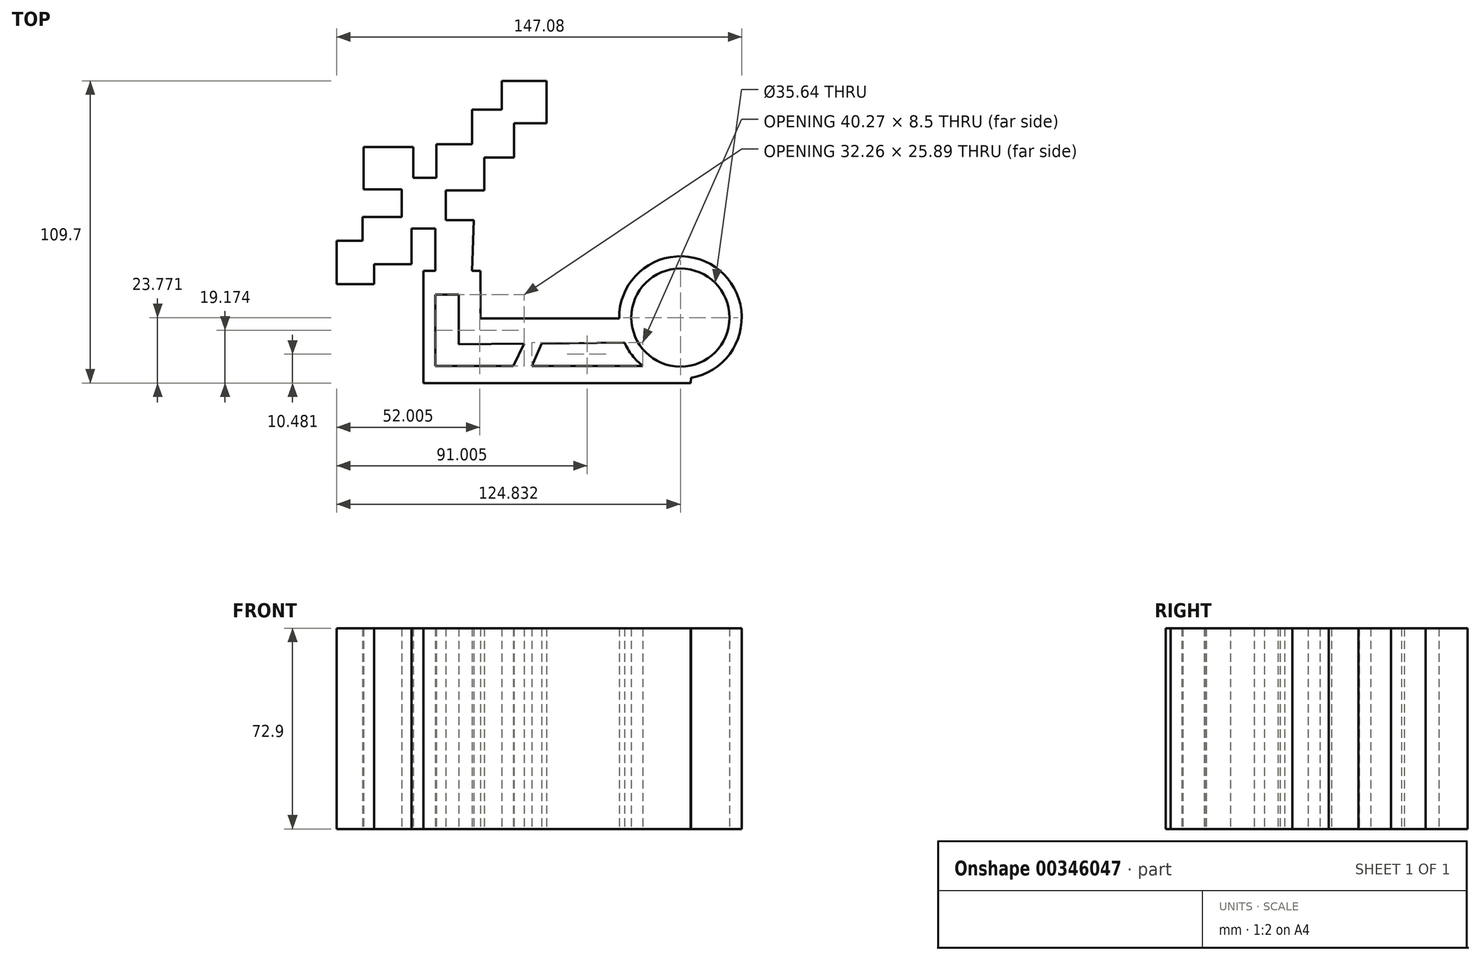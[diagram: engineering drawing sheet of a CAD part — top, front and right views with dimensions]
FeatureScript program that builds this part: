
annotation { "Feature Type Name" : "Feature", "Feature Type Description" : "" }
export const myFeature = defineFeature(function(context is Context, id is Id, definition is map)
    precondition{}
    {
        {
            var Q0;
            Q0=qCreatedBy(makeId("Top.planeOp"),FACE);
            var sketch = newSketch(context, id + "F0", { "sketchPlane" : qUnion([Q0])});
            skLineSegment(sketch, "E0.bottom", {"start": v(16.37, 58.04) * mm, "end": v(0, 58.04) * mm});
            skLineSegment(sketch, "E0.top", {"start": v(16.37, 42.71) * mm, "end": v(4.52, 42.71) * mm});
            skLineSegment(sketch, "E0.left", {"start": v(16.37, 58.04) * mm, "end": v(16.37, 42.71) * mm});
            skLineSegment(sketch, "E0.right", {"start": v(0, 58.04) * mm, "end": v(0, 47.59) * mm});
            skLineSegment(sketch, "E1.bottom", {"start": v(0, 47.59) * mm, "end": v(-10.8, 47.59) * mm});
            skLineSegment(sketch, "E1.top", {"start": v(4.52, 30.17) * mm, "end": v(-6.27, 30.17) * mm});
            skLineSegment(sketch, "E1.left", {"start": v(4.52, 42.71) * mm, "end": v(4.52, 30.17) * mm});
            skLineSegment(sketch, "E1.right", {"start": v(-10.8, 47.59) * mm, "end": v(-10.8, 35.05) * mm});
            skLineSegment(sketch, "E2.bottom", {"start": v(-10.8, 35.05) * mm, "end": v(-23.69, 35.05) * mm});
            skLineSegment(sketch, "E2.top", {"start": v(-6.27, 18.33) * mm, "end": v(-10.1, 18.33) * mm});
            skLineSegment(sketch, "E2.left", {"start": v(-6.27, 30.17) * mm, "end": v(-6.27, 18.33) * mm});
            skPoint(sketch, "E3.oppositeSnap0", {"position": v(-23.69, 26.7) * mm});
            skLineSegment(sketch, "E3.left", {"start": v(-23.69, 26.7) * mm, "end": v(-23.69, 26.7) * mm});
            skLineSegment(sketch, "E3.right", {"start": v(-30.65, 26.7) * mm, "end": v(-30.65, 26.7) * mm});
            skLineSegment(sketch, "E4.bottom", {"start": v(-20.2, 18.33) * mm, "end": v(-10.1, 18.33) * mm});
            skPoint(sketch, "E5.orphan", {"position": v(-27.17, 18.33) * mm});
            skPoint(sketch, "E4.right.end.orphan", {"position": v(-10.1, 0) * mm});
            skLineSegment(sketch, "E6", {"start": v(-23.69, 35.05) * mm, "end": v(-23.69, 22.86) * mm});
            skLineSegment(sketch, "E7.bottom", {"start": v(-23.69, 22.86) * mm, "end": v(-32.04, 22.86) * mm});
            skLineSegment(sketch, "E7.top", {"start": v(-24.03, 4.4) * mm, "end": v(-32.74, 4.4) * mm});
            skLineSegment(sketch, "E7.left", {"start": v(-20.2, 18.33) * mm, "end": v(-20.2, 7.54) * mm});
            skLineSegment(sketch, "E7.right", {"start": v(-36.22, 18.68) * mm, "end": v(-36.22, 8.58) * mm});
            skPoint(sketch, "E8.orphan", {"position": v(-53.29, 41.32) * mm});
            skPoint(sketch, "E9.top.end.orphan", {"position": v(-53.29, 34) * mm});
            skPoint(sketch, "E9.bottom.start.orphan", {"position": v(-44.93, 26.7) * mm});
            skPoint(sketch, "E10.bottom.end.orphan", {"position": v(-53.29, 26.7) * mm});
            skPoint(sketch, "E10.left.start.orphan", {"position": v(-36.57, 26.7) * mm});
            skPoint(sketch, "E11.left.start.orphan", {"position": v(-15.68, 4.4) * mm});
            skPoint(sketch, "E11.right.end.orphan", {"position": v(0, -11.27) * mm});
            skLineSegment(sketch, "E12.bottom", {"start": v(-20.2, 7.54) * mm, "end": v(-7.32, 7.54) * mm});
            skLineSegment(sketch, "E12.top", {"start": v(-7.67, -10.9) * mm, "end": v(-7.32, -10.9) * mm});
            skLineSegment(sketch, "E12.left", {"start": v(-24.03, 4.4) * mm, "end": v(-24.03, -10.9) * mm});
            skLineSegment(sketch, "E13.bottom", {"start": v(-36.22, 18.68) * mm, "end": v(-50.15, 18.68) * mm});
            skLineSegment(sketch, "E13.top", {"start": v(-32.04, 34) * mm, "end": v(-50.15, 34) * mm});
            skLineSegment(sketch, "E13.left", {"start": v(-32.04, 22.86) * mm, "end": v(-32.04, 34) * mm});
            skLineSegment(sketch, "E13.right", {"start": v(-50.15, 18.68) * mm, "end": v(-50.15, 34) * mm});
            skLineSegment(sketch, "E14.bottom", {"start": v(-36.22, 8.58) * mm, "end": v(-50.5, 8.58) * mm});
            skLineSegment(sketch, "E14.top", {"start": v(-32.74, -8.48) * mm, "end": v(-46.32, -8.48) * mm});
            skLineSegment(sketch, "E14.left", {"start": v(-32.74, 4.4) * mm, "end": v(-32.74, -8.48) * mm});
            skLineSegment(sketch, "E14.right", {"start": v(-50.5, 8.58) * mm, "end": v(-50.5, 0.05) * mm});
            skPoint(sketch, "E15.firstSnap0", {"position": v(-32.74, 0.05) * mm});
            skLineSegment(sketch, "E15.bottom", {"start": v(-50.5, 0.05) * mm, "end": v(-59.9, 0.05) * mm});
            skLineSegment(sketch, "E15.top", {"start": v(-46.32, -15.8) * mm, "end": v(-59.9, -15.8) * mm});
            skLineSegment(sketch, "E15.left", {"start": v(-46.32, -8.48) * mm, "end": v(-46.32, -15.8) * mm});
            skLineSegment(sketch, "E15.right", {"start": v(-59.9, 0.05) * mm, "end": v(-59.9, -15.8) * mm});
            skPoint(sketch, "E16.orphan", {"position": v(-36.22, 4.4) * mm});
            skPoint(sketch, "E17.orphan", {"position": v(0, 42.71) * mm});
            skPoint(sketch, "E18.orphan", {"position": v(-23.69, 18.33) * mm});
            skPoint(sketch, "E19.orphan", {"position": v(-32.74, 8.58) * mm});
            skPoint(sketch, "E20.orphan", {"position": v(-46.32, 0.05) * mm});
            skLineSegment(sketch, "E21.top", {"start": v(-24.03, -45.43) * mm, "end": v(-7.67, -45.43) * mm});
            skLineSegment(sketch, "E21.left", {"start": v(-24.03, -19.54) * mm, "end": v(-24.03, -45.43) * mm});
            skLineSegment(sketch, "E21.right", {"start": v(-7.67, -10.9) * mm, "end": v(-7.67, -28.16) * mm});
            skLineSegment(sketch, "E22.bottom", {"start": v(-7.67, -28.16) * mm, "end": v(42.67, -28.16) * mm});
            skLineSegment(sketch, "E22.top", {"start": v(-7.67, -45.43) * mm, "end": v(51.23, -45.43) * mm});
            skPoint(sketch, "E23.orphan", {"position": v(50.84, -10.9) * mm});
            skPoint(sketch, "E24.top.end.orphan", {"position": v(69.3, -45.43) * mm});
            skCircle(sketch, "E25", {"center": v(64.92, -27.89) * mm, "radius": 22.25 * mm});
            skCircle(sketch, "E26", {"center": v(64.92, -27.89) * mm, "radius": 17.82 * mm});
            skPoint(sketch, "E27.trimOffspring.end.orphan", {"position": v(50.84, -28.16) * mm});
            skLineSegment(sketch, "E28", {"start": v(-28.39, -10.9) * mm, "end": v(-28.39, -46.79) * mm});
            skLineSegment(sketch, "E29", {"start": v(-28.39, -46.79) * mm, "end": v(-28.39, -51.66) * mm});
            skLineSegment(sketch, "E30", {"start": v(-28.39, -51.66) * mm, "end": v(68.58, -51.66) * mm});
            skLineSegment(sketch, "E31", {"start": v(68.58, -51.66) * mm, "end": v(68.8, -49.8) * mm});
            skLineSegment(sketch, "E32", {"start": v(-10.1, 7.54) * mm, "end": v(-10.8, -10.9) * mm});
            skLineSegment(sketch, "E33", {"start": v(-24.03, -10.9) * mm, "end": v(-10.8, -10.9) * mm});
            skLineSegment(sketch, "E34", {"start": v(-28.39, -10.9) * mm, "end": v(-7.32, -10.9) * mm});
            skPoint(sketch, "E35.orphan", {"position": v(-28.39, 4.4) * mm});
            skPoint(sketch, "E36", {"position": v(-7.67, -19.53) * mm});
            skPoint(sketch, "E37.trimOffspring.start.orphan", {"position": v(-11.12, -19.53) * mm});
            skLineSegment(sketch, "E38", {"start": v(-15.54, -32.46) * mm, "end": v(-15.54, -19.54) * mm});
            skLineSegment(sketch, "E39", {"start": v(-15.54, -19.54) * mm, "end": v(-24.03, -19.54) * mm});
            skLineSegment(sketch, "E40", {"start": v(-15.54, -32.46) * mm, "end": v(-15.54, -37.64) * mm});
            skLineSegment(sketch, "E41", {"start": v(-15.54, -37.64) * mm, "end": v(44.59, -36.93) * mm});
            skLineSegment(sketch, "E42", {"start": v(8.22, -37.36) * mm, "end": v(4.25, -45.43) * mm});
            skLineSegment(sketch, "E43", {"start": v(14.52, -37.29) * mm, "end": v(10.96, -45.43) * mm});
            skPoint(sketch, "E44.start.orphan", {"position": v(16.37, 73.91) * mm});
            skPoint(sketch, "E45.start.orphan", {"position": v(20.42, 73.91) * mm});
            skSolve(sketch);
        }
        {
            var Q0;
            Q0=makeQuery(id+"F0.imprint","IMPRINT",FACE,{"disambiguationData":[TD([[makeQuery(id+"F0.imprint","IMPRINT",EDGE,{"derivedFrom":sQuery(id+"F0.wireOp",EDGE,"E0.bottom")}),1.0]])]});
            var Q1;
            {var subQ11=sQuery(id+"F0.wireOp",EDGE,"E21.top");Q1=makeQuery(id+"F0.imprint","IMPRINT",FACE,{"disambiguationData":[TD([[makeQuery(id+"F0.imprint","IMPRINT",EDGE,{"derivedFrom":subQ11}),-1.0]])]});}
            var Q2;
            Q2=makeQuery(id+"F0.imprint","IMPRINT",FACE,{"disambiguationData":[TD([[makeQuery(id+"F0.imprint","IMPRINT",EDGE,{"derivedFrom":sQuery(id+"F0.wireOp",EDGE,"E26")}),-1.0]])]});
            var Q3;
            {var subQ0=sQuery(id+"F0.wireOp",EDGE,"E42");Q3=makeQuery(id+"F0.imprint","IMPRINT",FACE,{"disambiguationData":[TD([[makeQuery(id+"F0.imprint","IMPRINT",EDGE,{"derivedFrom":subQ0}),1.0]])]});}
            extrude(context, id + "F1", {"entities" : qUnion([Q0, Q1, Q2, Q3]), "depth" : 72.9 * mm});
        }
    });
